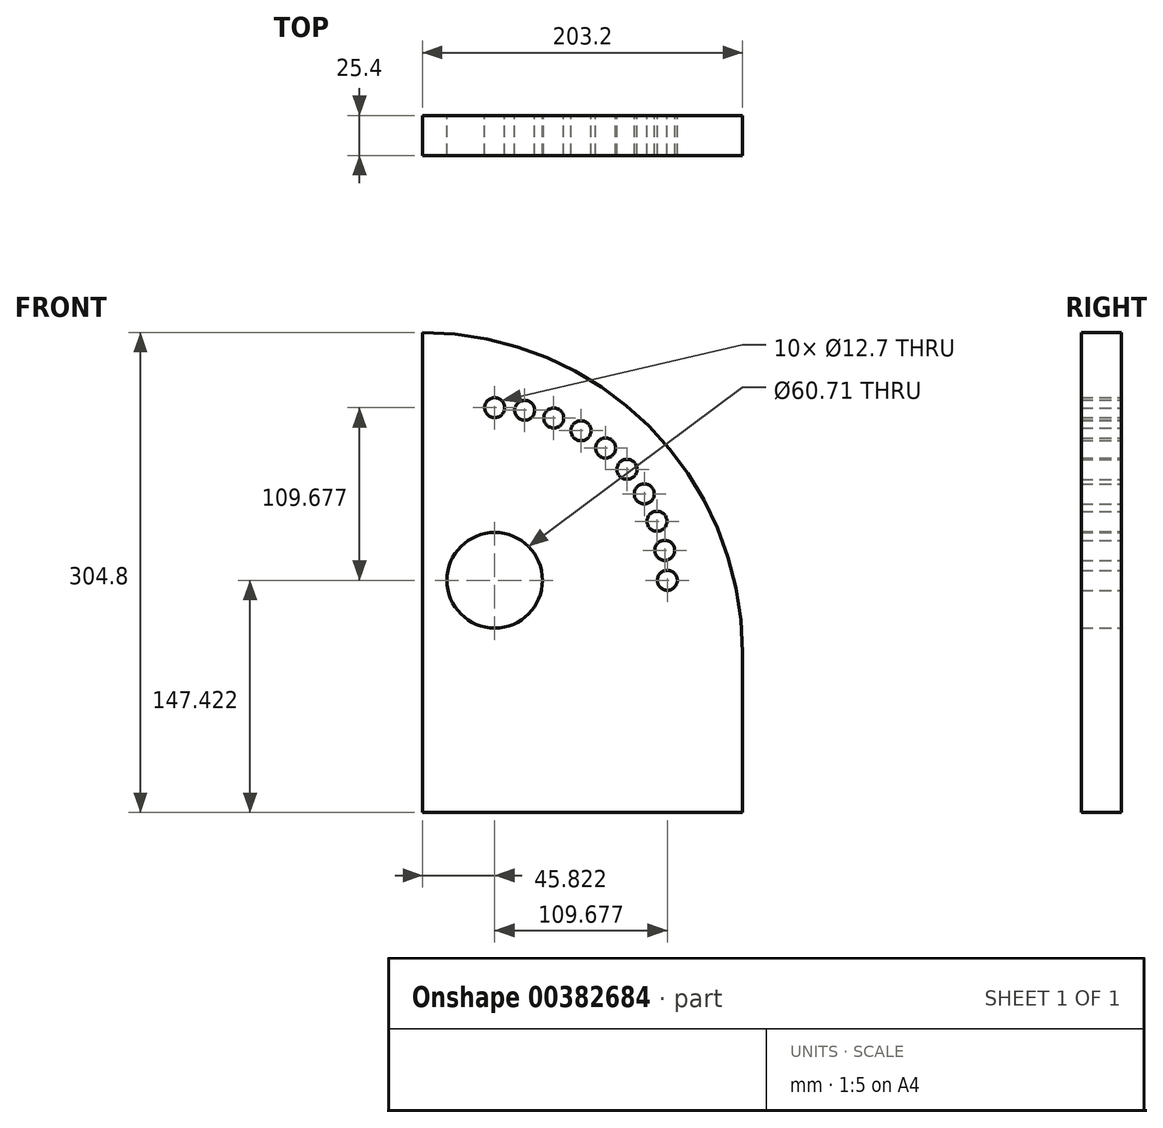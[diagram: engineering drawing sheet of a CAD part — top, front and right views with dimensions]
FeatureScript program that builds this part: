
annotation { "Feature Type Name" : "Feature", "Feature Type Description" : "" }
export const myFeature = defineFeature(function(context is Context, id is Id, definition is map)
    precondition{}
    {
        {
            var Q0;
            Q0=qCreatedBy(makeId("Front.planeOp"),FACE);
            var sketch = newSketch(context, id + "F0", { "sketchPlane" : qUnion([Q0])});
            skLineSegment(sketch, "E0.left", {"start": v(0, 0) * mm, "end": v(0, 203.2) * mm});
            skLineSegment(sketch, "E1.0", {"start": v(45.82, -4.98) * mm, "end": v(45.82, 401.42) * mm, "construction": true});
            skLineSegment(sketch, "E2.0", {"start": v(-22.61, 45.82) * mm, "end": v(180.59, 45.82) * mm, "construction": true});
            skCircle(sketch, "E3", {"center": v(45.82, 45.82) * mm, "radius": 30.35 * mm});
            skCircle(sketch, "E4", {"center": v(155.5, 45.82) * mm, "radius": 6.35 * mm});
            skCircle(sketch, "E5.1.0", {"center": v(153.83, 64.87) * mm, "radius": 6.35 * mm});
            skCircle(sketch, "E5.2.0", {"center": v(148.88, 83.33) * mm, "radius": 6.35 * mm});
            skCircle(sketch, "E5.3.0", {"center": v(140.8, 100.66) * mm, "radius": 6.35 * mm});
            skCircle(sketch, "E5.4.0", {"center": v(129.84, 116.32) * mm, "radius": 6.35 * mm});
            skCircle(sketch, "E5.5.0", {"center": v(116.32, 129.84) * mm, "radius": 6.35 * mm});
            skCircle(sketch, "E5.6.0", {"center": v(100.66, 140.8) * mm, "radius": 6.35 * mm});
            skCircle(sketch, "E5.7.0", {"center": v(83.33, 148.88) * mm, "radius": 6.35 * mm});
            skCircle(sketch, "E5.8.0", {"center": v(64.87, 153.83) * mm, "radius": 6.35 * mm});
            skCircle(sketch, "E5.9.0", {"center": v(45.82, 155.5) * mm, "radius": 6.35 * mm});
            skLineSegment(sketch, "E5.anchor1", {"start": v(45.82, 45.82) * mm, "end": v(155.5, 45.82) * mm, "construction": true});
            skLineSegment(sketch, "E5.anchor2", {"start": v(45.82, 45.82) * mm, "end": v(45.82, 155.5) * mm, "construction": true});
            skArc(sketch, "E6", {"start": v(203.2, 0) * mm, "mid": v(143.68, 143.68) * mm, "end": v(0, 203.2) * mm});
            skSolve(sketch);
        }
        {
            var Q0;
            Q0=makeQuery(id+"F0.imprint","IMPRINT",FACE,{"disambiguationData":[TD([[makeQuery(id+"F0.imprint","IMPRINT",EDGE,{"derivedFrom":sQuery(id+"F0.wireOp",EDGE,"E3")}),1.0]])]});
            var sketch = newSketch(context, id + "F1", { "sketchPlane" : qUnion([Q0])});
            skLineSegment(sketch, "E7.bottom", {"start": v(0, 0) * mm, "end": v(203.2, 0) * mm});
            skLineSegment(sketch, "E7.top", {"start": v(0, -101.6) * mm, "end": v(203.2, -101.6) * mm});
            skLineSegment(sketch, "E7.left", {"start": v(0, 0) * mm, "end": v(0, -101.6) * mm});
            skLineSegment(sketch, "E7.right", {"start": v(203.2, 0) * mm, "end": v(203.2, -101.6) * mm});
            skArc(sketch, "E8.0", {"start": v(203.2, 0) * mm, "mid": v(143.68, 143.68) * mm, "end": v(0, 203.2) * mm});
            skSolve(sketch);
        }
        {
            var Q0;
            Q0=qCreatedBy(makeId("Front.planeOp"),FACE);
            var sketch = newSketch(context, id + "F2", { "sketchPlane" : qUnion([Q0])});
            skLineSegment(sketch, "E9.0", {"start": v(0, 0) * mm, "end": v(0, 203.2) * mm});
            skPoint(sketch, "E10.0", {"position": v(45.82, 198.22) * mm});
            skArc(sketch, "E11.0", {"start": v(203.2, 0) * mm, "mid": v(143.68, 143.68) * mm, "end": v(0, 203.2) * mm});
            skLineSegment(sketch, "E12.0", {"start": v(0, 0) * mm, "end": v(203.2, 0) * mm});
            skLineSegment(sketch, "E13.0.0", {"start": v(0, 0) * mm, "end": v(0, -101.6) * mm});
            skLineSegment(sketch, "E13.0.1", {"start": v(0, -101.6) * mm, "end": v(203.2, -101.6) * mm});
            skLineSegment(sketch, "E13.0.2", {"start": v(203.2, -101.6) * mm, "end": v(203.2, 0) * mm});
            skLineSegment(sketch, "E13.0.3", {"start": v(203.2, 0) * mm, "end": v(0, 0) * mm});
            skCircle(sketch, "E14.0", {"center": v(45.82, 45.82) * mm, "radius": 30.35 * mm});
            skCircle(sketch, "E15.0", {"center": v(155.5, 45.82) * mm, "radius": 6.35 * mm});
            skCircle(sketch, "E16.0", {"center": v(153.83, 64.87) * mm, "radius": 6.35 * mm});
            skCircle(sketch, "E17.0", {"center": v(148.88, 83.33) * mm, "radius": 6.35 * mm});
            skCircle(sketch, "E18.0", {"center": v(140.8, 100.66) * mm, "radius": 6.35 * mm});
            skCircle(sketch, "E19.0", {"center": v(129.84, 116.32) * mm, "radius": 6.35 * mm});
            skCircle(sketch, "E20.0", {"center": v(116.32, 129.84) * mm, "radius": 6.35 * mm});
            skCircle(sketch, "E21.0", {"center": v(100.66, 140.8) * mm, "radius": 6.35 * mm});
            skPoint(sketch, "E22.0", {"position": v(83.33, 148.88) * mm});
            skCircle(sketch, "E23.0", {"center": v(83.33, 148.88) * mm, "radius": 6.35 * mm});
            skPoint(sketch, "E24.0", {"position": v(64.87, 153.83) * mm});
            skCircle(sketch, "E25.0", {"center": v(64.87, 153.83) * mm, "radius": 6.35 * mm});
            skCircle(sketch, "E26.0", {"center": v(45.82, 155.5) * mm, "radius": 6.35 * mm});
            skSolve(sketch);
        }
        {
            var Q0;
            Q0 = qSketchRegion(id + "F2", true);
            extrude(context, id + "F3", {"entities" : qUnion([Q0]), "depth" : 25.4 * mm});
        }
    });
